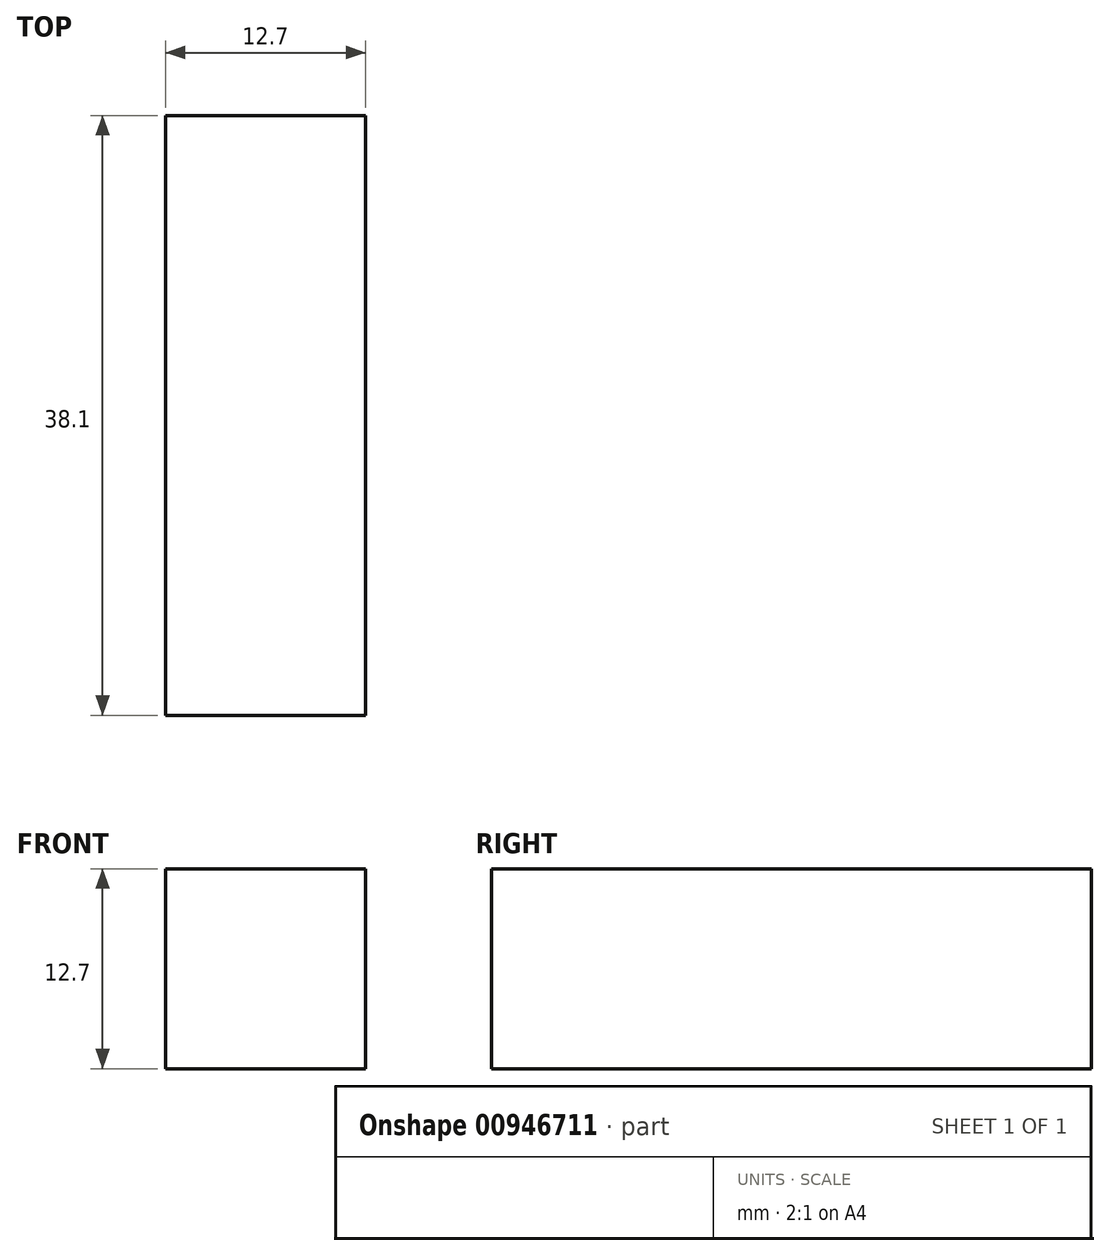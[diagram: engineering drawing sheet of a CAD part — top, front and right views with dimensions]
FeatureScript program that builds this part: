
annotation { "Feature Type Name" : "Feature", "Feature Type Description" : "" }
export const myFeature = defineFeature(function(context is Context, id is Id, definition is map)
    precondition{}
    {
        {
            var Q0;
            Q0=qCreatedBy(makeId("Front.planeOp"),FACE);
            var sketch = newSketch(context, id + "F0", { "sketchPlane" : qUnion([Q0])});
            skLineSegment(sketch, "E0.bottom", {"start": v(6.35, 6.35) * mm, "end": v(-6.35, 6.35) * mm});
            skLineSegment(sketch, "E0.top", {"start": v(6.35, -6.35) * mm, "end": v(-6.35, -6.35) * mm});
            skLineSegment(sketch, "E0.left", {"start": v(6.35, 6.35) * mm, "end": v(6.35, -6.35) * mm});
            skLineSegment(sketch, "E0.right", {"start": v(-6.35, 6.35) * mm, "end": v(-6.35, -6.35) * mm});
            skPoint(sketch, "E0.middle", {"position": v(0, 0) * mm});
            skSolve(sketch);
        }
        {
            var Q0;
            Q0 = qSketchRegion(id + "F0", true);
            extrude(context, id + "F1", {"entities" : qUnion([Q0]), "depth" : 38.1 * mm, "offsetDistance" : 25.4 * mm});
        }
    });
